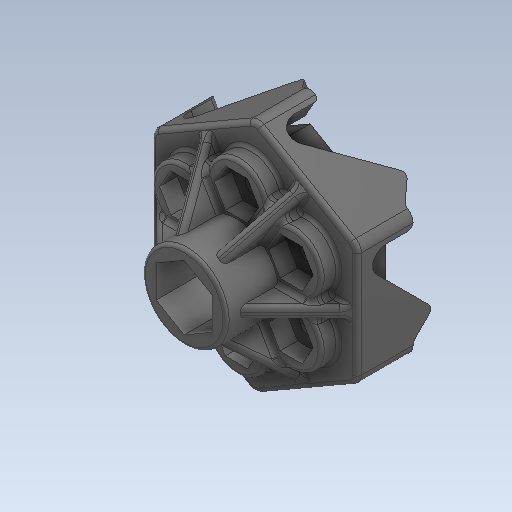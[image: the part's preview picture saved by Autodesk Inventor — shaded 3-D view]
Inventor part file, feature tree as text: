
AUTODESK INVENTOR PART (.ipt)
format: ipt  version: 2020 (Build 240168000, 168)  size: 1,298,432 bytes
history: native  units: in
note: dims shown in document units (in); Inventor stores cm internally (conversion verified against a paired STEP export)
features: fillet x1
ambient origin geometry x8: Origin, YZ Plane, XZ Plane, XY Plane, X Axis, Y Axis, Z Axis, Center Point
bodies: Solid1 (feature_tree)
feature tree (1):
  fillet  "Fillet21"  [1 undecoded]
note: 1 required parameter value undecoded (feature->parameter linkage not recoverable at this tier; creation-order binding heuristic only, values carry confidence <= 0.55)
